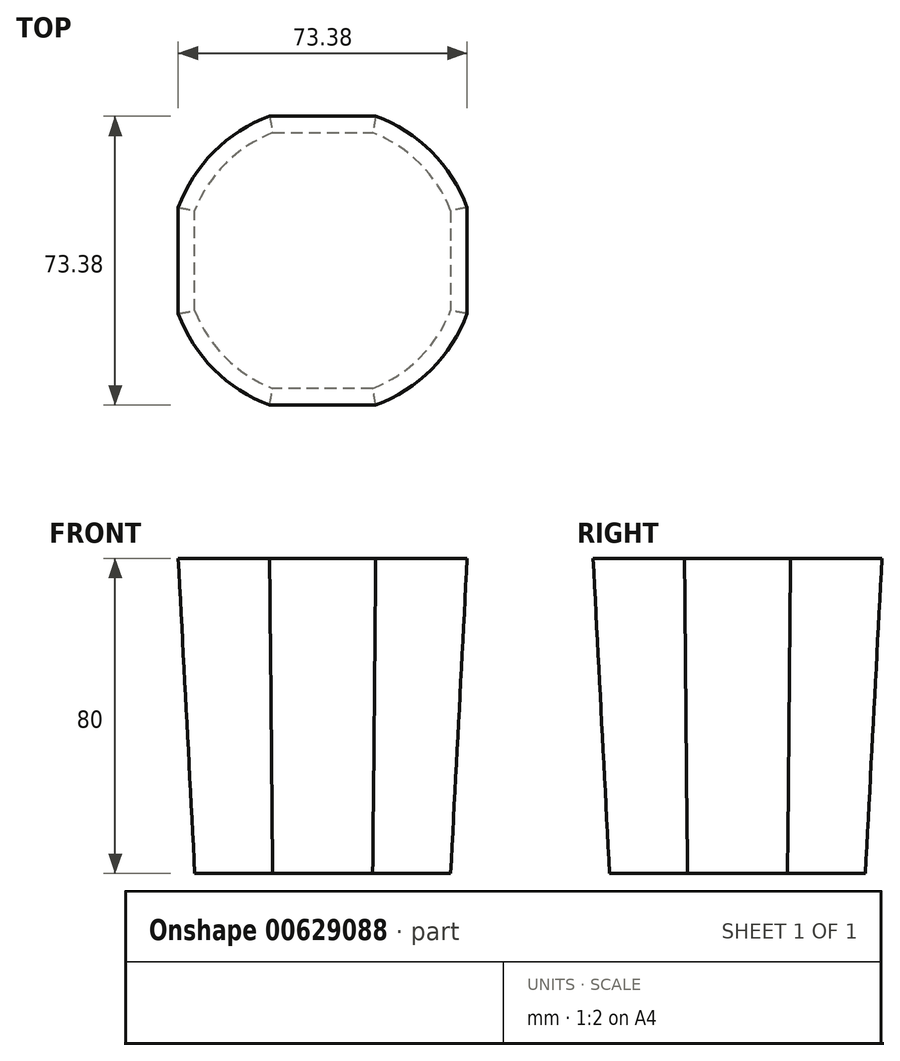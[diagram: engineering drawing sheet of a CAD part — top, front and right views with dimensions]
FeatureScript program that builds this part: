
annotation { "Feature Type Name" : "Feature", "Feature Type Description" : "" }
export const myFeature = defineFeature(function(context is Context, id is Id, definition is map)
    precondition{}
    {
        {
            var Q0;
            Q0=qCreatedBy(makeId("Top.planeOp"),FACE);
            var sketch = newSketch(context, id + "F0", { "sketchPlane" : qUnion([Q0])});
            skLineSegment(sketch, "E0.bottom", {"start": v(-12.71, 32.5) * mm, "end": v(12.71, 32.5) * mm});
            skLineSegment(sketch, "E0.top", {"start": v(-12.71, -32.5) * mm, "end": v(12.71, -32.5) * mm});
            skLineSegment(sketch, "E0.left", {"start": v(-32.5, 12.71) * mm, "end": v(-32.5, -12.71) * mm});
            skLineSegment(sketch, "E0.right", {"start": v(32.5, 12.71) * mm, "end": v(32.5, -12.71) * mm});
            skPoint(sketch, "E0.middle", {"position": v(0, 0) * mm});
            skArc(sketch, "E1", {"start": v(12.71, -32.5) * mm, "mid": v(24.68, -24.68) * mm, "end": v(32.5, -12.71) * mm});
            skPoint(sketch, "E2", {"position": v(-32.5, 12.71) * mm});
            skPoint(sketch, "E3", {"position": v(-32.5, -12.71) * mm});
            skPoint(sketch, "E4", {"position": v(32.5, -12.71) * mm});
            skPoint(sketch, "E5", {"position": v(32.5, 12.71) * mm});
            skPoint(sketch, "E6", {"position": v(12.71, -32.5) * mm});
            skPoint(sketch, "E7", {"position": v(-12.71, -32.5) * mm});
            skPoint(sketch, "E8", {"position": v(-12.71, 32.5) * mm});
            skPoint(sketch, "E9", {"position": v(12.71, 32.5) * mm});
            skArc(sketch, "E10.trimOffspring", {"start": v(-12.71, 32.5) * mm, "mid": v(-24.68, 24.68) * mm, "end": v(-32.5, 12.71) * mm});
            skArc(sketch, "E11.trimOffspring", {"start": v(-32.5, -12.71) * mm, "mid": v(-24.68, -24.68) * mm, "end": v(-12.71, -32.5) * mm});
            skArc(sketch, "E12.trimOffspring", {"start": v(32.5, 12.71) * mm, "mid": v(24.68, 24.68) * mm, "end": v(12.71, 32.5) * mm});
            skSolve(sketch);
        }
        {
            var Q0;
            Q0 = qSketchRegion(id + "F0", true);
            extrude(context, id + "F1", {"entities" : qUnion([Q0]), "depth" : 80 * mm, "hasOffset" : true, "offsetDistance" : 25 * mm, "hasDraft" : true, "draftAngle" : 3 * degree});
        }
    });
